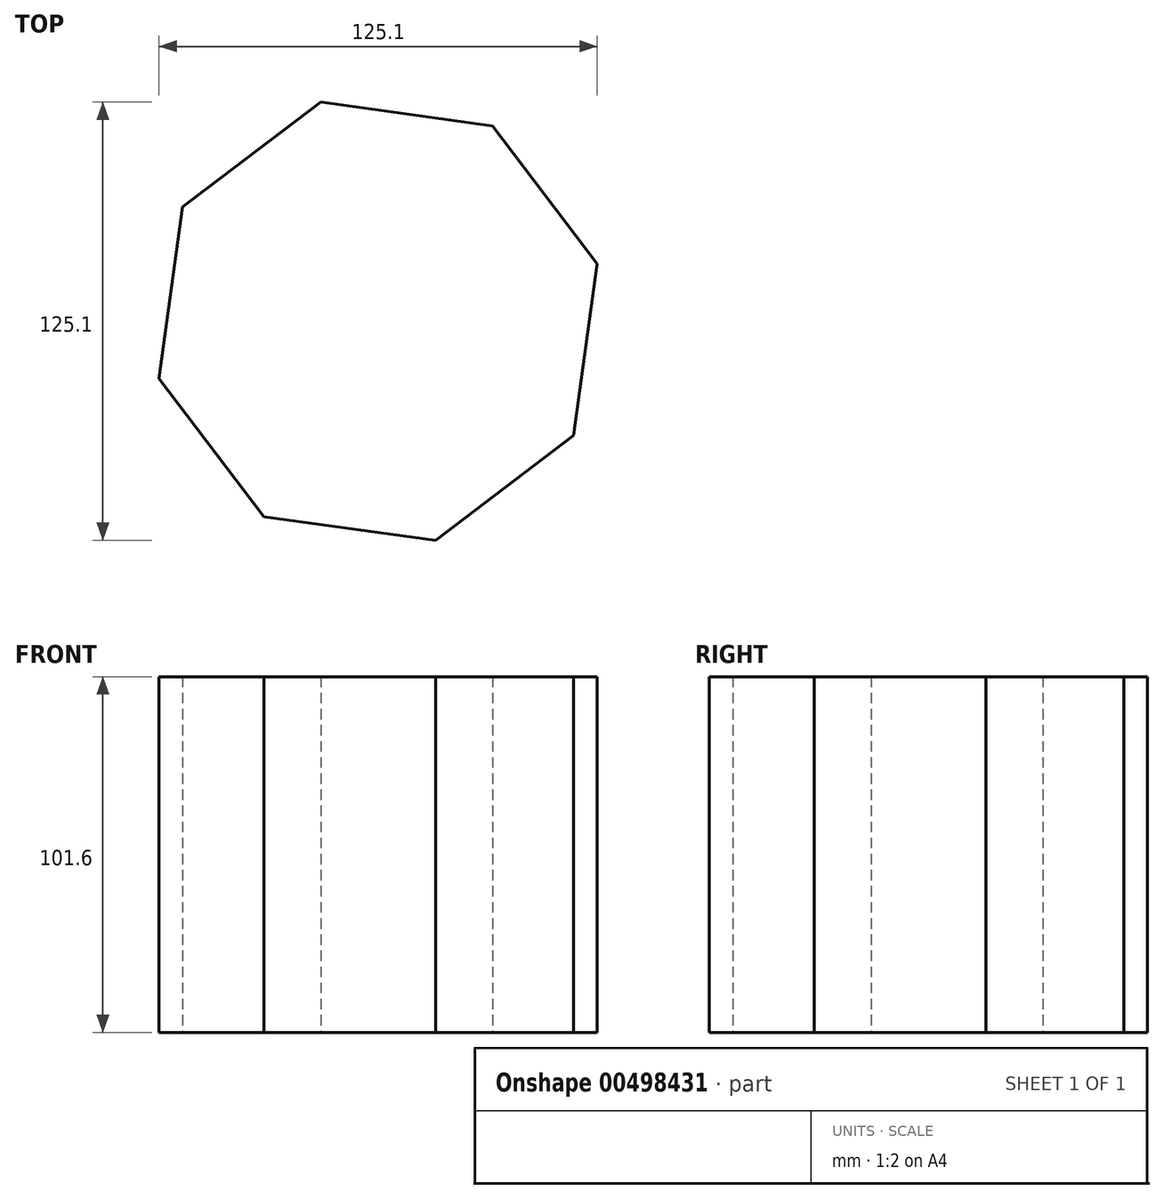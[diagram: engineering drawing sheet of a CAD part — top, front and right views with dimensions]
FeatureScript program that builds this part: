
annotation { "Feature Type Name" : "Feature", "Feature Type Description" : "" }
export const myFeature = defineFeature(function(context is Context, id is Id, definition is map)
    precondition{}
    {
        {
            var Q0;
            Q0=qCreatedBy(makeId("Top.planeOp"),FACE);
            var sketch = newSketch(context, id + "F0", { "sketchPlane" : qUnion([Q0])});
            skCircle(sketch, "E0.cCircle", {"center": v(0, 0) * mm, "radius": 64.66 * mm, "construction": true});
            skLineSegment(sketch, "E0.0", {"start": v(32.65, 55.82) * mm, "end": v(62.55, 16.39) * mm});
            skLineSegment(sketch, "E0.1", {"start": v(62.55, 16.39) * mm, "end": v(55.82, -32.65) * mm});
            skLineSegment(sketch, "E0.2", {"start": v(55.82, -32.65) * mm, "end": v(16.39, -62.55) * mm});
            skLineSegment(sketch, "E0.3", {"start": v(16.39, -62.55) * mm, "end": v(-32.65, -55.82) * mm});
            skLineSegment(sketch, "E0.4", {"start": v(-32.65, -55.82) * mm, "end": v(-62.55, -16.39) * mm});
            skLineSegment(sketch, "E0.5", {"start": v(-62.55, -16.39) * mm, "end": v(-55.82, 32.65) * mm});
            skLineSegment(sketch, "E0.6", {"start": v(-55.82, 32.65) * mm, "end": v(-16.39, 62.55) * mm});
            skLineSegment(sketch, "E0.7", {"start": v(-16.39, 62.55) * mm, "end": v(32.65, 55.82) * mm});
            skSolve(sketch);
        }
        {
            var Q0;
            Q0=makeQuery(id+"F0.imprint","IMPRINT",FACE,{"disambiguationData":[TD([[makeQuery(id+"F0.imprint","IMPRINT",EDGE,{"derivedFrom":sQuery(id+"F0.wireOp",EDGE,"E0.0")}),-1.0]])]});
            extrude(context, id + "F1", {"entities" : qUnion([Q0]), "depth" : 101.6 * mm, "offsetDistance" : 25.4 * mm});
        }
    });
